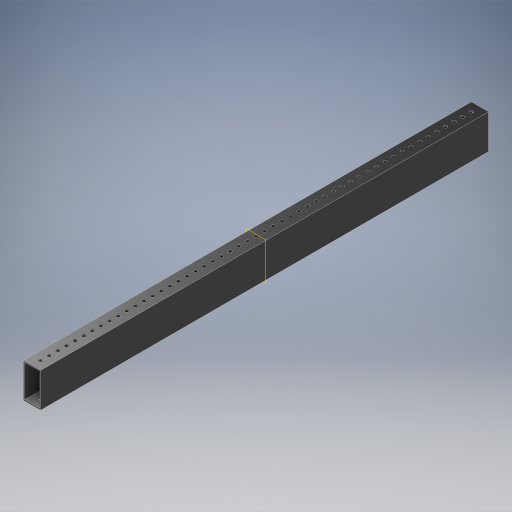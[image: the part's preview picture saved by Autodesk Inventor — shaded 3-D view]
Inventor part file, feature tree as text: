
AUTODESK INVENTOR PART (.ipt)
format: ipt  version: 2024.2 (Build 282272000, 272)  size: 836,608 bytes
history: native  units: in
note: dims shown in document units (in); Inventor stores cm internally (conversion verified against a paired STEP export)
features: other x13, extrude x10, hole x3, pattern_linear x3, mirror x3, plane x2, sheet_metal_op x1, sketch x1
ambient origin geometry x8: Origin, YZ Plane, XZ Plane, XY Plane, X Axis, Y Axis, Z Axis, Center Point
bodies: Solid1 (feature_tree)
feature tree (36):
  other  "Blocks"
  other  "Base Sketch"
  extrude  "Base"  Depth=1.0in
  extrude  "MAX Corner"  Depth=0.0625in
  extrude  "MAX Corner Cut"  Depth=0.0625in
  extrude  "Scribe Lines"  Depth=1.0in
  other  "Side Middle"
  other  "Top Middle"
  other  "Side Holes Sketch"
  hole  "Top Side Hole"  [1 undecoded]
  hole  "Mid Side Hole"  [1 undecoded]
  hole  "Btm Side Hole"  [1 undecoded]
  pattern_linear  "Side Holes"  Spacing1=0.04in  [1 undecoded]
  mirror  "Side Mirror"
  extrude  "MAXTube Hole"  Depth=26.0in
  extrude  "MAXTube Outside"  TaperAngle=0.0deg  [1 undecoded]
  pattern_linear  "MAXTube Pattern"  Spacing1=26.0in  [1 undecoded]
  mirror  "MAXTube Mirror"
  extrude  "Left Top Hole"  TaperAngle=0.0deg  [1 undecoded]
  extrude  "Mid Top Hole"  TaperAngle=0.0deg  [1 undecoded]
  extrude  "Right Top Hole"  Depth=1.0in
  pattern_linear  "Top Holes"  Spacing1=0.0in  [1 undecoded]
  mirror  "Top Mirror"
  extrude  "Extrusion11"  Depth=1.0in
  plane  "Work Plane5"
  sheet_metal_op  "Corner"
  other  "MAXTube"
  plane  "Work Plane3"
  sketch  "Sketch5"  dims[d0=2.0in d1=1.0in d2=0.0625in d3=0.0625in d4=0.4375in d5=0.04in d6=0.0671in d7=0.0272in d8=0.0in d9=0.0in d10=0.0in d11=0.085in d12=0.085in d16=0.04in d17=0.04in d18=0.04in d19=0.04in d20=26.0in d21=0.0in d22=26.0in d23=0.0in d24=0.0in d25=0.0in d26=0.005in d30=0.0in d31=0.0in d34=0.5in d35=0.5in d38=0.5in d40=0.196in d41=0.75in d42=0.375in d43=0.25in d44=0.5635in d45=1.0in d46=0.8108in d47=0.196in d48=0.75in d49=0.375in d50=0.25in d51=0.5635in d52=1.0in d53=0.8108in d54=0.196in d55=0.75in d56=0.375in d57=0.25in d58=0.5635in d59=1.0in d60=0.8108in d61=0.5in d62=0.3937in d64=2.0in d69=1.5in d70=0.0in d71=0.0in d72=2.7559in d74=2.0in d78=2.0in d79=-13.0in d80=0.196in d81=0.0in d82=0.0in d83=0.5in d84=0.0in d85=0.0in d86=0.0in d87=0.0in d88=0.0in d89=0.0in d90=10.2362in d92=0.5in d93=1.0in d95=0.0in d96=0.0in d97=0.5in d98=24.0in d100=-13.0in d101=0.25in d102=0.25in d103=0.25in d104=0.25in d105=0.5in d106=0.0in]
  other  "Corner:5"
  other  "Corner:6"
  other  "Corner:7"
  other  "Corner:8"
  other  "MAXTube:1"
  other  "MAXTube:2"
  other  "MAXTube:3"
note: 9 required parameter values undecoded (feature->parameter linkage not recoverable at this tier; creation-order binding heuristic only, values carry confidence <= 0.55)
